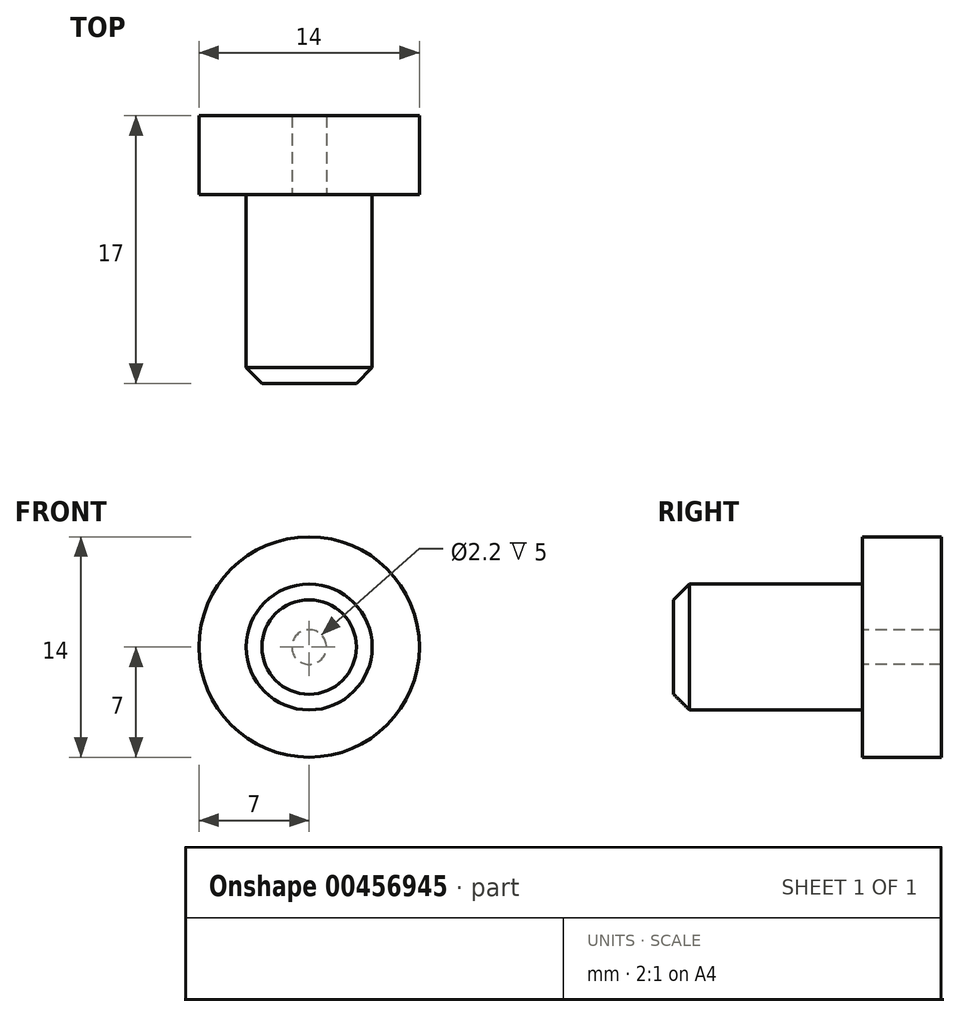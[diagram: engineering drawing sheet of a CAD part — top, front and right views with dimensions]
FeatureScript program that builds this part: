
annotation { "Feature Type Name" : "Feature", "Feature Type Description" : "" }
export const myFeature = defineFeature(function(context is Context, id is Id, definition is map)
    precondition{}
    {
        {
            var Q0;
            Q0=qCreatedBy(makeId("Front.planeOp"),FACE);
            var sketch = newSketch(context, id + "F0", { "sketchPlane" : qUnion([Q0])});
            skCircle(sketch, "E0", {"center": v(0, 0) * mm, "radius": 7 * mm});
            skSolve(sketch);
        }
        {
            var Q0;
            Q0 = qSketchRegion(id + "F0", true);
            extrude(context, id + "F1", {"entities" : qUnion([Q0]), "depth" : 5 * mm});
        }
        {
            var Q0;
            Q0=makeQuery(id+"F1.opExtrude","CAP_FACE",FACE,{"disambiguationData":[OSD([sQuery(id+"F0.wireOp",EDGE,"E0")])],"isStart":false});
            var sketch = newSketch(context, id + "F2", { "sketchPlane" : qUnion([Q0])});
            skCircle(sketch, "E1", {"center": v(0, 0) * mm, "radius": 1.1 * mm});
            skSolve(sketch);
        }
        {
            var Q0;
            Q0 = qSketchRegion(id + "F2", true);
            extrude(context, id + "F3", {"entities" : qUnion([Q0]), "operationType" : NewBodyOperationType.REMOVE, "endBound" : BoundingType.THROUGH_ALL, "oppositeDirection" : true, "depth" : 25 * mm});
        }
        {
            var Q0;
            Q0=makeQuery(id+"F1.opExtrude","CAP_FACE",FACE,{"disambiguationData":[OSD([sQuery(id+"F0.wireOp",EDGE,"E0")])],"isStart":false});
            var sketch = newSketch(context, id + "F4", { "sketchPlane" : qUnion([Q0])});
            skCircle(sketch, "E2", {"center": v(0, 0) * mm, "radius": 4 * mm});
            skSolve(sketch);
        }
        {
            var Q0;
            Q0 = qSketchRegion(id + "F4", true);
            extrude(context, id + "F5", {"entities" : qUnion([Q0]), "operationType" : NewBodyOperationType.ADD, "depth" : 12 * mm});
        }
        {
            var Q0;
            Q0=makeQuery(id+"F5.opExtrude","CAP_EDGE",EDGE,{"disambiguationData":[OSD([sQuery(id+"F4.wireOp",EDGE,"E2")])],"isStart":false});
            var Q1;
            Q1=makeQuery(id+"F5.opExtrude","CAP_EDGE",EDGE,{"disambiguationData":[OSD([sQuery(id+"F4.wireOp",EDGE,"E2")])],"isStart":true});
            chamfer(context, id + "F6", {"entities" : qUnion([Q0, Q1]), "width" : 1 * mm, "tangentPropagation" : true});
        }
    });
